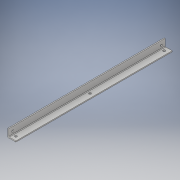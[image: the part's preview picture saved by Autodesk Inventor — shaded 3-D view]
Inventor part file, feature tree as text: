
AUTODESK INVENTOR PART (.ipt)
format: ipt  version: 2017 (Build 210142000, 142)  size: 131,072 bytes
history: native  units: in
note: dims shown in document units (in); Inventor stores cm internally (conversion verified against a paired STEP export)
features: sketch x4, hole x3, extrude x1
ambient origin geometry x8: Origin, YZ Plane, XZ Plane, XY Plane, X Axis, Y Axis, Z Axis, Center Point
bodies: Solid1 (feature_tree)
feature tree (8):
  extrude  "Extrusion1"  Depth=1.0in
  hole  "Hole1"  [1 undecoded]
  hole  "Hole2"  [1 undecoded]
  hole  "Hole3"  [1 undecoded]
  sketch  "Sketch1"  dims[d0=1.0in d1=1.0in]
  sketch  "Sketch2"  dims[d2=0.125in d3=19.375in d4=0.0in]
  sketch  "Sketch5"  dims[d5=0.5in d6=0.5in]
  sketch  "Sketch6"  dims[d7=0.7874in d9=18.375in d10=0.3937in d12=1.0in d14=0.281in d15=0.75in d16=0.385in d17=0.25in d18=0.5635in d19=1.0in d20=0.8108in d21=0.07in d24=0.281in d25=0.75in d26=0.385in d27=0.25in d28=0.5635in d29=1.0in d30=0.8108in d31=0.5in d32=0.5in d33=0.5in d34=18.375in d35=0.5in d36=0.281in d37=0.75in d38=0.385in d39=0.25in d40=0.5635in d41=1.0in d42=0.8108in]
note: 3 required parameter values undecoded (feature->parameter linkage not recoverable at this tier; creation-order binding heuristic only, values carry confidence <= 0.55)
